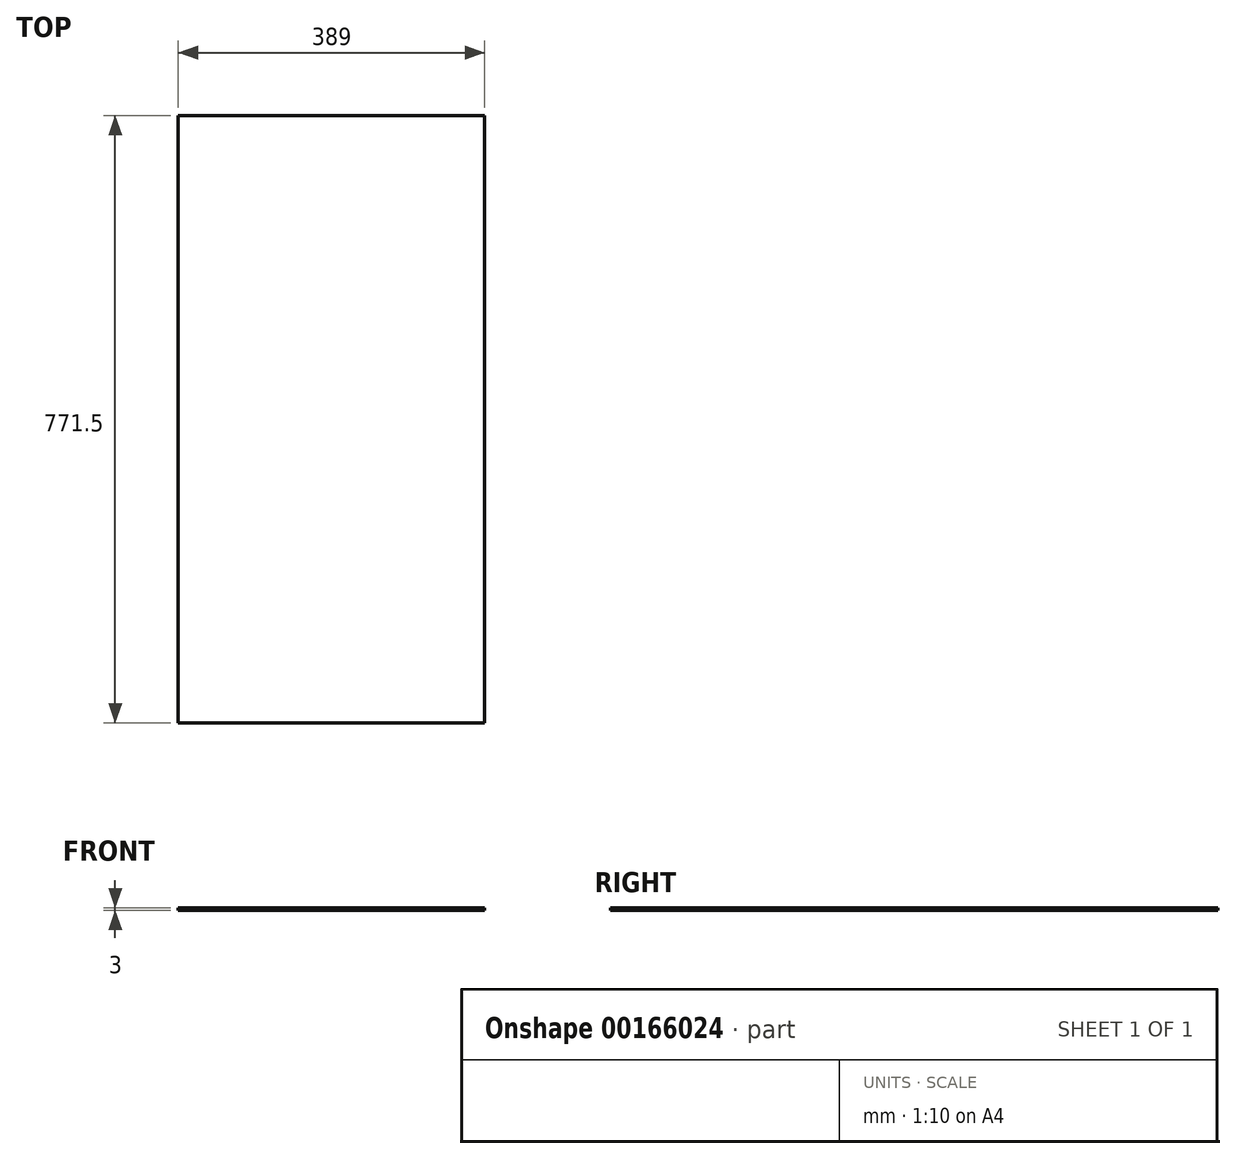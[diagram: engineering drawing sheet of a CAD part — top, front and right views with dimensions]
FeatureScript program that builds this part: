
annotation { "Feature Type Name" : "Feature", "Feature Type Description" : "" }
export const myFeature = defineFeature(function(context is Context, id is Id, definition is map)
    precondition{}
    {
        {
            var Q0;
            Q0=qCreatedBy(makeId("Top.planeOp"),FACE);
            var sketch = newSketch(context, id + "F0", { "sketchPlane" : qUnion([Q0])});
            skLineSegment(sketch, "E0.bottom", {"start": v(0, 0) * mm, "end": v(389, 0) * mm});
            skLineSegment(sketch, "E0.top", {"start": v(0, 771.5) * mm, "end": v(389, 771.5) * mm});
            skLineSegment(sketch, "E0.left", {"start": v(0, 0) * mm, "end": v(0, 771.5) * mm});
            skLineSegment(sketch, "E0.right", {"start": v(389, 0) * mm, "end": v(389, 771.5) * mm});
            skSolve(sketch);
        }
        {
            var Q0;
            Q0=makeQuery(id+"F0.imprint","IMPRINT",FACE,{"disambiguationData":[TD([[makeQuery(id+"F0.imprint","IMPRINT",EDGE,{"derivedFrom":sQuery(id+"F0.wireOp",EDGE,"E0.bottom")}),1.0]])]});
            extrude(context, id + "F1", {"entities" : qUnion([Q0]), "depth" : 3 * mm});
        }
    });
